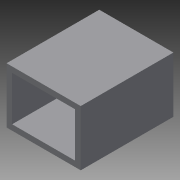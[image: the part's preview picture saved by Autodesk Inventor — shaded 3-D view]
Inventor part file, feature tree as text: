
AUTODESK INVENTOR PART (.ipt)
format: ipt  version: 2013 (Build 170138000, 138)  size: 79,872 bytes
history: native  units: mm
features: extrude x2, sketch x2, other x1
ambient origin geometry x8: Origin, YZ Plane, XZ Plane, XY Plane, X Axis, Y Axis, Z Axis, Center Point
feature tree (5):
  other  "ソリッド1"
  extrude  "押し出し1"  Depth=40.0mm
  extrude  "押し出し2"  Depth=30.0mm
  sketch  "スケッチ1"
  sketch  "スケッチ2"
